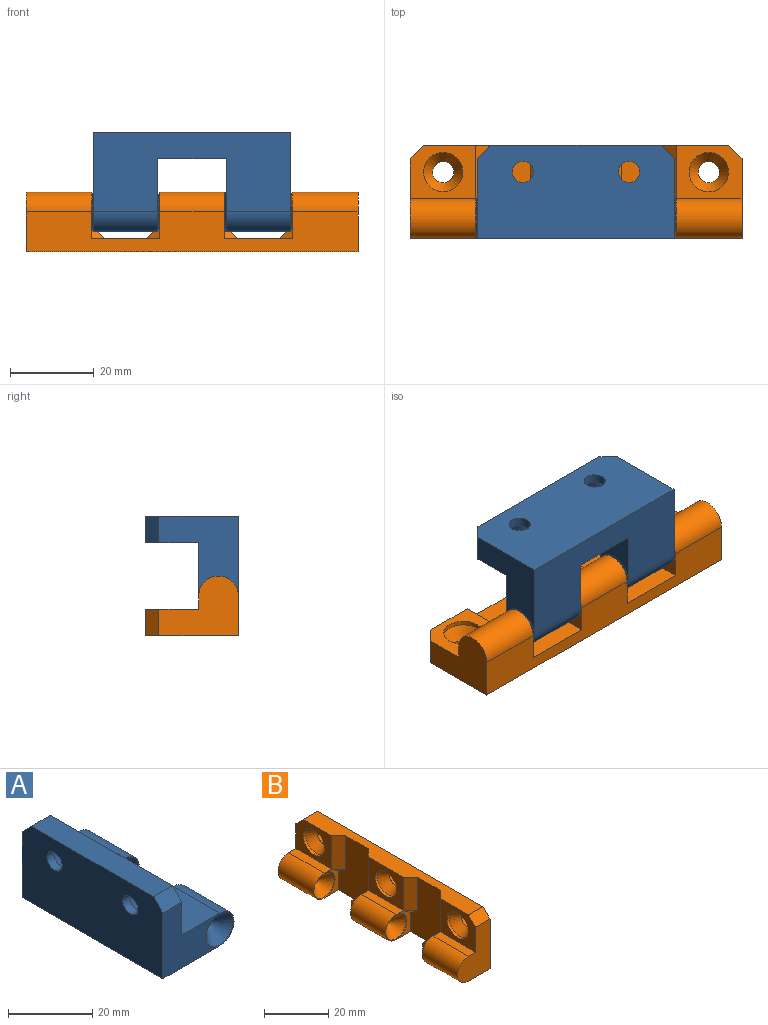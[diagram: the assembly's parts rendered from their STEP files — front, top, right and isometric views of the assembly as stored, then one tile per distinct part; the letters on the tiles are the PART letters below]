
ASSEMBLY  parts=2 mates=1
PART A: 32 faces, bbox 24.5x51.3x22.9 mm
  f0: plane 15.48x12.7mm, normal (0,0,1), area 196.6mm2, adj f5,f6,f7,f9
  f1: plane 15.48x12.7mm, normal (0,0,1), area 196.6mm2, adj f2,f3,f4,f9
  f2: cylinder r=4.76mm len=15.48mm, axis (0,-1,0), area 231.6mm2, adj f1,f10,f16,f18
  f3: plane 12.7x9.53mm, normal (0,1,0), area 85.3mm2, adj f1,f9,f10,f18
  f4: plane 19.05x19.05mm, normal (0,-1,0), area 206.3mm2, adj f1,f8,f9,f10,f16,f30
  f5: cylinder r=4.76mm len=15.48mm, axis (0,-1,0), area 231.6mm2, adj f0,f10,f11,f21
  f6: plane 19.05x19.05mm, normal (0,1,0), area 206.3mm2, adj f0,f8,f9,f10,f21,f31
  f7: plane 12.7x9.53mm, normal (0,-1,0), area 85.3mm2, adj f0,f9,f10,f11
  f8: plane 47.23x22.23mm, normal (-1,0,0), area 999mm2, adj f4,f6,f10,f23,f24,f27,f30,f31
  f9: plane 47.23x22.23mm, normal (1,0,0), area 606mm2, adj f0,f1,f3,f4,f6,f7,f10,f23
  f10: plane 47.23x19.05mm, normal (0,0,-1), area 693mm2, adj f2,f3,f4,f5,f6,f7,f8,f9
  f11: torus R=4.76mm, axis (0,1,0), area 9mm2, adj f5,f7,f13
  f12: sphere r=1.19mm, area 2.6mm2, adj f13
  f13: cone r=4.48mm half-angle=45deg, axis (0,-1,0), area 86.1mm2, adj f11,f12
  f14: sphere r=1.19mm, area 2.6mm2, adj f15
  f15: cone r=4.48mm half-angle=45deg, axis (0,-1,0), area 86.1mm2, adj f14,f16
  f16: torus R=4.76mm, axis (0,1,0), area 9mm2, adj f2,f4,f15
  f17: cone r=4.2mm half-angle=45deg, axis (0,-1,0), area 77mm2, adj f18,f19
  f18: torus R=4.76mm, axis (0,-1,0), area 17.5mm2, adj f2,f3,f17
  f19: sphere r=0.79mm, area 1.2mm2, adj f17
  f20: cone r=4.2mm half-angle=45deg, axis (0,-1,0), area 77mm2, adj f21,f22
  f21: torus R=4.76mm, axis (0,-1,0), area 17.5mm2, adj f5,f6,f20
  f22: sphere r=0.79mm, area 1.2mm2, adj f20
  f23: plane 40.88x6.35mm, normal (0,0,1), area 259.6mm2, adj f8,f9,f30,f31
  f24: cylinder r=2.54mm len=5.08mm, axis (1,0,0), area 35.9mm2, adj f8,f25
  f25: cone r=4.7mm half-angle=35deg, axis (1,0,0), area 85.6mm2, adj f24,f26
  f26: cylinder r=4.7mm len=9.4mm, axis (1,0,0), area 30mm2, adj f9,f25
  f27: cylinder r=2.54mm len=5.08mm, axis (1,0,0), area 35.9mm2, adj f8,f28
  f28: cone r=4.7mm half-angle=35deg, axis (1,0,0), area 85.6mm2, adj f27,f29
  f29: cylinder r=4.7mm len=9.4mm, axis (1,0,0), area 30mm2, adj f9,f28
  f30: plane 6.35x3.18mm, normal (0,-0.71,0.71), area 28.5mm2, adj f4,f8,f9,f23
  f31: plane 6.35x3.18mm, normal (0,0.71,0.71), area 28.5mm2, adj f6,f8,f9,f23
PART B: 51 faces, bbox 15x79.4x22.9 mm
  f0: plane 22.23x16.27mm, normal (-1,0,0), area 273.9mm2, adj f1,f4,f18,f31,f43,f44,f49,f50
  f1: plane 9.53x6.35mm, normal (0,1,0), area 21.3mm2, adj f0,f3,f11,f18,f49
  f2: cone r=4.2mm half-angle=45deg, axis (0,-1,0), area 77mm2, adj f3,f26
  f3: torus R=4.76mm, axis (0,-1,0), area 17.5mm2, adj f1,f2,f12
  f4: plane 9.53x6.35mm, normal (0,-1,0), area 21.3mm2, adj f0,f18,f19,f20,f50
  f5: plane 22.23x16.27mm, normal (-1,0,0), area 273.9mm2, adj f6,f9,f18,f31,f45,f46,f47,f48
  f6: plane 9.53x6.35mm, normal (0,1,0), area 21.3mm2, adj f5,f8,f18,f19,f48
  f7: cone r=4.2mm half-angle=45deg, axis (0,-1,0), area 77mm2, adj f8,f27
  f8: torus R=4.76mm, axis (0,-1,0), area 17.5mm2, adj f6,f7,f14
  f9: plane 9.53x6.35mm, normal (0,-1,0), area 21.3mm2, adj f5,f10,f18,f23,f47
  f10: plane 15.68x3.18mm, normal (0,0,1), area 49.8mm2, adj f9,f13,f16,f28
  f11: plane 15.68x3.18mm, normal (0,0,1), area 49.8mm2, adj f1,f12,f15,f30
  f12: cylinder r=4.76mm len=15.68mm, axis (0,-1,0), area 234.6mm2, adj f3,f11,f15,f18
  f13: cylinder r=4.76mm len=15.68mm, axis (0,-1,0), area 234.6mm2, adj f10,f16,f18,f23
  f14: cylinder r=4.76mm len=15.48mm, axis (0,-1,0), area 231.6mm2, adj f8,f18,f19,f20
  f15: plane 19.05x14.29mm, normal (0,-1,0), area 186.8mm2, adj f11,f12,f17,f18,f30,f42
  f16: plane 19.05x14.29mm, normal (0,1,0), area 186.8mm2, adj f10,f13,f17,f18,f28,f41
  f17: plane 79.38x22.23mm, normal (1,0,0), area 1693.2mm2, adj f15,f16,f18,f31,f32,f35,f38,f41
  f18: plane 79.38x9.53mm, normal (0,0,-1), area 549.4mm2, adj f0,f1,f4,f5,f6,f9,f12,f13
  f19: plane 15.48x3.18mm, normal (0,0,1), area 49.1mm2, adj f4,f6,f14,f29
  f20: torus R=4.76mm, axis (0,1,0), area 9mm2, adj f4,f14,f22
  f21: sphere r=1.19mm, area 2.6mm2, adj f22
  f22: cone r=4.48mm half-angle=45deg, axis (0,-1,0), area 86.1mm2, adj f20,f21
  f23: torus R=4.76mm, axis (0,1,0), area 9mm2, adj f9,f13,f25
  f24: sphere r=1.19mm, area 2.6mm2, adj f25
  f25: cone r=4.48mm half-angle=45deg, axis (0,-1,0), area 86.1mm2, adj f23,f24
  f26: sphere r=0.79mm, area 1.2mm2, adj f2
  f27: sphere r=0.79mm, area 1.2mm2, adj f7
  f28: plane 15.68x12.7mm, normal (-1,0,0), area 124.7mm2, adj f10,f16,f31,f40,f41,f46
  f29: plane 15.48x12.7mm, normal (-1,0,0), area 127.2mm2, adj f19,f31,f37,f44,f45
  f30: plane 15.68x12.7mm, normal (-1,0,0), area 124.7mm2, adj f11,f15,f31,f34,f42,f43
  f31: plane 73.03x6.35mm, normal (0,0,1), area 380.5mm2, adj f0,f5,f17,f28,f29,f30,f41,f42
  f32: cylinder r=2.54mm len=5.08mm, axis (-1,0,0), area 35.9mm2, adj f17,f33
  f33: cone r=4.7mm half-angle=35deg, axis (-1,0,0), area 85.6mm2, adj f32,f34
  f34: cylinder r=4.7mm len=9.4mm, axis (-1,0,0), area 30mm2, adj f30,f33
  f35: cylinder r=2.54mm len=5.08mm, axis (-1,0,0), area 35.9mm2, adj f17,f36
  f36: cone r=4.7mm half-angle=35deg, axis (-1,0,0), area 85.6mm2, adj f35,f37
  f37: cylinder r=4.7mm len=9.4mm, axis (-1,0,0), area 30mm2, adj f29,f36
  f38: cylinder r=2.54mm len=5.08mm, axis (-1,0,0), area 35.9mm2, adj f17,f39
  f39: cone r=4.7mm half-angle=35deg, axis (-1,0,0), area 85.6mm2, adj f38,f40
  f40: cylinder r=4.7mm len=9.4mm, axis (-1,0,0), area 30mm2, adj f28,f39
  f41: plane 6.35x3.18mm, normal (0,0.71,0.71), area 28.5mm2, adj f16,f17,f28,f31
  f42: plane 6.35x3.18mm, normal (0,-0.71,0.71), area 28.5mm2, adj f15,f17,f30,f31
  f43: plane 12.7x3.18mm, normal (-0.71,0.71,0), area 57mm2, adj f0,f30,f31,f49
  f44: plane 12.7x3.18mm, normal (-0.71,-0.71,0), area 57mm2, adj f0,f29,f31,f50
  f45: plane 12.7x3.18mm, normal (-0.71,0.71,0), area 57mm2, adj f5,f29,f31,f48
  f46: plane 12.7x3.18mm, normal (-0.71,-0.71,0), area 57mm2, adj f5,f28,f31,f47
  f47: plane 3.18x3.18mm, normal (-0.5,-0.5,-0.71), area 7.1mm2, adj f5,f9,f46
  f48: plane 3.18x3.18mm, normal (-0.5,0.5,-0.71), area 7.1mm2, adj f5,f6,f45
  f49: plane 3.18x3.18mm, normal (-0.5,0.5,-0.71), area 7.1mm2, adj f0,f1,f43
  f50: plane 3.18x3.18mm, normal (-0.5,-0.5,-0.71), area 7.1mm2, adj f0,f4,f44
PLACE A rot(axis=(-0.58,0.58,0.58),120deg) t=(39.69,-6.06,-19.05)mm
PLACE B rot(axis=(-0.58,0.58,0.58),120deg) t=(39.69,-6.06,-19.05)mm
MATE revolute A.f11 <-> B.f12  axis (1,0,0) through (23.61,-6.06,-19.05)mm
